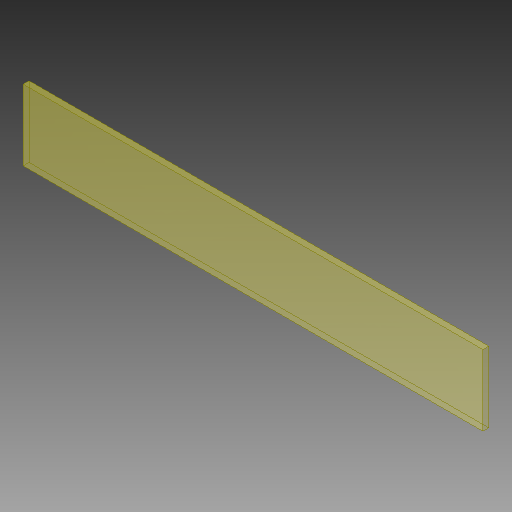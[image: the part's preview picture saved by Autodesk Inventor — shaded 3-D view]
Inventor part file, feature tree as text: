
AUTODESK INVENTOR PART (.ipt)
format: ipt  version: 2018.1 (Build 221171000, 171)  size: 91,648 bytes
history: native  units: mm
features: other x1, extrude x1, sketch x1
ambient origin geometry x8: Origin, YZ Plane, XZ Plane, XY Plane, X Axis, Y Axis, Z Axis, Center Point
bodies: Solid1 (feature_tree)
feature tree (3):
  parser-record x1  (decoder bookkeeping rows leaked as tree rows — omitted from the tree; the rows remain in map.json)
  extrude  "Extrusion1"  Depth=60.0mm
  sketch  "Sketch1"  dims[d0=390.0mm d1=60.0mm d2=5.0mm d3=0.0mm]
note: 1 file-system path scrubbed to <path> (originals preserved in map.json)
